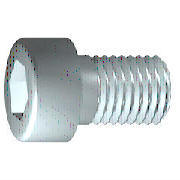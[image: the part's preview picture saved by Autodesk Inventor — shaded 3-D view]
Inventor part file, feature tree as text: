
AUTODESK INVENTOR PART (.ipt)
format: ipt  version: 2019 (Build 230136000, 136)  size: 205,824 bytes
history: native  units: mm (DEFAULTED — no unit token found)
features: sketch x2, extrude x1, plane x1, fillet x1
ambient origin geometry x7: Origin, YZ Plane, XY Plane, X Axis, Y Axis, Z Axis, Center Point
bodies: Solid1 (feature_tree), Body (feature_tree)
feature tree (5):
  extrude  "Slot"  Depth=8.0mm
  plane  "Work Plane1"
  fillet  "Fillet2"  Radius=8.0mm
  sketch  "Sketch1"  dims[d1=16.875mm d2=0.766912mm d3=8.0mm]
  sketch  "Sketch2"  dims[d4=4.0mm d5=60.0deg d6=8.0mm d7=8.0mm d8=6.928203mm d9=13.0mm d10=90.0deg d11=10.0mm d12=0.0mm d13=16.875mm d14=0.0mm d15=0.766813mm d16=0.766813mm d17=0.8mm d19=0.0mm d26=20.0mm d27=45.0deg d28=0.0mm d29=0.0mm d30=0.1mm]
